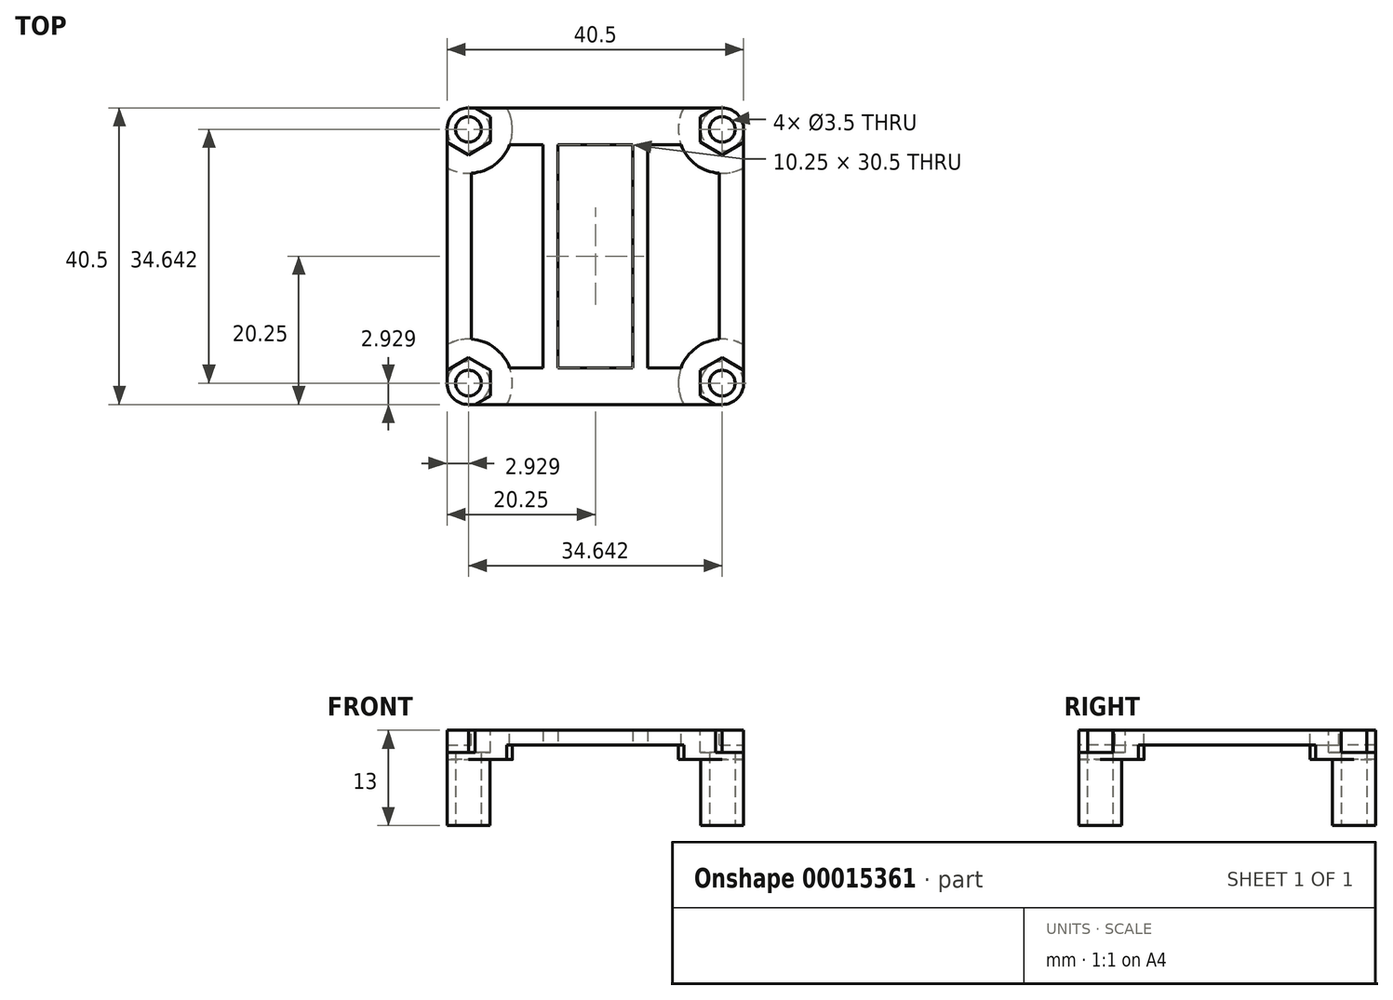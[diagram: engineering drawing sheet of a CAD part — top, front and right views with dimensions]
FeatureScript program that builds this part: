
annotation { "Feature Type Name" : "Feature", "Feature Type Description" : "" }
export const myFeature = defineFeature(function(context is Context, id is Id, definition is map)
    precondition{}
    {
        {
            var Q0;
            Q0=qCreatedBy(makeId("Top.planeOp"),FACE);
            var sketch = newSketch(context, id + "F0", { "sketchPlane" : qUnion([Q0])});
            skLineSegment(sketch, "E0.bottom", {"start": v(2.93, 0) * mm, "end": v(37.57, 0) * mm});
            skLineSegment(sketch, "E0.top", {"start": v(2.93, 40.5) * mm, "end": v(37.57, 40.5) * mm});
            skLineSegment(sketch, "E0.left", {"start": v(0, 2.93) * mm, "end": v(0, 37.57) * mm});
            skLineSegment(sketch, "E0.right", {"start": v(40.5, 2.93) * mm, "end": v(40.5, 37.57) * mm});
            skLineSegment(sketch, "E1", {"start": v(2.93, 0) * mm, "end": v(5, 0) * mm, "construction": true});
            skLineSegment(sketch, "E2", {"start": v(5, 0) * mm, "end": v(5, 5) * mm, "construction": true});
            skLineSegment(sketch, "E3", {"start": v(40.5, 0) * mm, "end": v(0, 40.5) * mm, "construction": true});
            skLineSegment(sketch, "E4.MirrorCS", {"start": v(40.5, 35.5) * mm, "end": v(35.5, 35.5) * mm, "construction": true});
            skLineSegment(sketch, "E5.MirrorCS", {"start": v(40.5, 37.57) * mm, "end": v(40.5, 35.5) * mm, "construction": true});
            skLineSegment(sketch, "E6.bottom", {"start": v(5, 5) * mm, "end": v(35.5, 5) * mm});
            skLineSegment(sketch, "E6.top", {"start": v(5, 35.5) * mm, "end": v(35.5, 35.5) * mm});
            skLineSegment(sketch, "E6.left", {"start": v(5, 5) * mm, "end": v(5, 35.5) * mm, "construction": true});
            skLineSegment(sketch, "E6.right", {"start": v(35.5, 5) * mm, "end": v(35.5, 35.5) * mm, "construction": true});
            skLineSegment(sketch, "E7", {"start": v(5, 35.5) * mm, "end": v(0, 40.5) * mm, "construction": true});
            skCircle(sketch, "E8", {"center": v(2.93, 37.57) * mm, "radius": 2.93 * mm});
            skLineSegment(sketch, "E9", {"start": v(35.5, 35.5) * mm, "end": v(40.5, 40.5) * mm, "construction": true});
            skLineSegment(sketch, "E10", {"start": v(35.5, 5) * mm, "end": v(40.5, 0) * mm, "construction": true});
            skLineSegment(sketch, "E11", {"start": v(5, 5) * mm, "end": v(0, 0) * mm, "construction": true});
            skCircle(sketch, "E12", {"center": v(37.57, 37.57) * mm, "radius": 2.93 * mm});
            skCircle(sketch, "E13", {"center": v(37.57, 2.93) * mm, "radius": 2.93 * mm});
            skCircle(sketch, "E14", {"center": v(2.93, 2.93) * mm, "radius": 2.93 * mm});
            skPoint(sketch, "E15.orphan", {"position": v(40.5, 40.5) * mm});
            skLineSegment(sketch, "E16", {"start": v(3.3, 34.67) * mm, "end": v(3.3, 5.83) * mm});
            skLineSegment(sketch, "E17", {"start": v(3.3, 8.58) * mm, "end": v(0, 8.58) * mm});
            skLineSegment(sketch, "E18", {"start": v(20.25, 40.5) * mm, "end": v(20.25, 0) * mm, "construction": true});
            skLineSegment(sketch, "E19.MirrorCS", {"start": v(37.2, 34.67) * mm, "end": v(37.2, 5.83) * mm});
            skSolve(sketch);
        }
        {
            var Q0;
            Q0=qSketchRegion(id+"F0",true);
            extrude(context, id + "F1", {"entities" : qUnion([Q0]), "depth" : 2 * mm});
        }
        {
            var Q0;
            Q0=makeQuery(id+"F1.opExtrude","CAP_FACE",FACE,{"disambiguationData":[OSD([sQuery(id+"F0.wireOp",EDGE,"E0.bottom"),sQuery(id+"F0.wireOp",EDGE,"E0.top"),sQuery(id+"F0.wireOp",EDGE,"E0.left"),sQuery(id+"F0.wireOp",EDGE,"E0.right"),sQuery(id+"F0.wireOp",EDGE,"E6.bottom"),sQuery(id+"F0.wireOp",EDGE,"E6.top"),sQuery(id+"F0.wireOp",EDGE,"E6.left"),sQuery(id+"F0.wireOp",EDGE,"E6.right"),sQuery(id+"F0.wireOp",EDGE,"E8"),sQuery(id+"F0.wireOp",EDGE,"E12"),sQuery(id+"F0.wireOp",EDGE,"E13"),sQuery(id+"F0.wireOp",EDGE,"E14")])],"isStart":false});
            var sketch = newSketch(context, id + "F2", { "sketchPlane" : qUnion([Q0])});
            skLineSegment(sketch, "E20", {"start": v(35.5, 35.5) * mm, "end": v(40.5, 35.5) * mm, "construction": true});
            skLineSegment(sketch, "E21", {"start": v(25.37, 0) * mm, "end": v(25.37, 17.5) * mm});
            skLineSegment(sketch, "E22", {"start": v(27.37, 0) * mm, "end": v(27.37, 17.5) * mm});
            skLineSegment(sketch, "E23", {"start": v(27.37, 40.5) * mm, "end": v(25.37, 40.5) * mm});
            skLineSegment(sketch, "E24", {"start": v(27.37, 0) * mm, "end": v(25.37, 0) * mm});
            skLineSegment(sketch, "E25", {"start": v(15.12, 0) * mm, "end": v(15.12, 17.5) * mm});
            skLineSegment(sketch, "E26", {"start": v(13.12, 0) * mm, "end": v(13.12, 17.5) * mm});
            skLineSegment(sketch, "E27", {"start": v(15.12, 0) * mm, "end": v(13.12, 0) * mm});
            skLineSegment(sketch, "E28.trimOffspring", {"start": v(25.37, 22.5) * mm, "end": v(25.37, 40.5) * mm});
            skLineSegment(sketch, "E29.trimOffspring", {"start": v(27.37, 22.5) * mm, "end": v(27.37, 40.5) * mm});
            skLineSegment(sketch, "E30", {"start": v(27.37, 5) * mm, "end": v(25.37, 5) * mm, "construction": true});
            skLineSegment(sketch, "E31", {"start": v(13.12, 17.5) * mm, "end": v(13.12, 22.5) * mm});
            skLineSegment(sketch, "E32", {"start": v(15.12, 22.5) * mm, "end": v(15.12, 17.5) * mm});
            skLineSegment(sketch, "E33", {"start": v(25.37, 17.5) * mm, "end": v(25.37, 22.5) * mm});
            skLineSegment(sketch, "E34", {"start": v(27.37, 22.5) * mm, "end": v(27.37, 17.5) * mm});
            skLineSegment(sketch, "E35", {"start": v(25.37, 0) * mm, "end": v(20.25, 0) * mm, "construction": true});
            skLineSegment(sketch, "E36", {"start": v(15.12, 0) * mm, "end": v(20.25, 0) * mm, "construction": true});
            skLineSegment(sketch, "E37", {"start": v(32.5, 0) * mm, "end": v(27.37, 0) * mm, "construction": true});
            skLineSegment(sketch, "E38", {"start": v(25.37, 0) * mm, "end": v(20.25, 0) * mm});
            skLineSegment(sketch, "E39", {"start": v(20.25, 0) * mm, "end": v(15.12, 0) * mm});
            skLineSegment(sketch, "E40", {"start": v(13.12, 0) * mm, "end": v(8, 0) * mm, "construction": true});
            skLineSegment(sketch, "E41", {"start": v(15.12, 22.5) * mm, "end": v(15.12, 40.5) * mm});
            skLineSegment(sketch, "E42", {"start": v(13.12, 22.5) * mm, "end": v(13.12, 40.5) * mm});
            skLineSegment(sketch, "E43", {"start": v(13.12, 40.5) * mm, "end": v(15.12, 40.5) * mm});
            skSolve(sketch);
        }
        {
            var Q0;
            Q0=qSketchRegion(id+"F2",true);
            extrude(context, id + "F3", {"entities" : qUnion([Q0]), "operationType" : NewBodyOperationType.ADD, "oppositeDirection" : true, "depth" : 2 * mm});
        }
        {
            var Q0;
            Q0=makeQuery(id+"F3.boolean.opBoolean","MERGE",FACE,{"derivedFrom":[makeQuery(id+"F1.opExtrude","CAP_FACE",FACE,{"disambiguationData":[OSD([sQuery(id+"F0.wireOp",EDGE,"E0.bottom"),sQuery(id+"F0.wireOp",EDGE,"E0.top"),sQuery(id+"F0.wireOp",EDGE,"E0.left"),sQuery(id+"F0.wireOp",EDGE,"E0.right"),sQuery(id+"F0.wireOp",EDGE,"E6.bottom"),sQuery(id+"F0.wireOp",EDGE,"E6.top"),sQuery(id+"F0.wireOp",EDGE,"E6.left"),sQuery(id+"F0.wireOp",EDGE,"E6.right"),sQuery(id+"F0.wireOp",EDGE,"E8"),sQuery(id+"F0.wireOp",EDGE,"E12"),sQuery(id+"F0.wireOp",EDGE,"E13"),sQuery(id+"F0.wireOp",EDGE,"E14")])],"isStart":true}),makeQuery(id+"F3.opExtrude","CAP_FACE",FACE,{"disambiguationData":[OSD([sQuery(id+"F2.wireOp",EDGE,"c7da8dac-bc2a-4405-bfd0-97204010a069"),sQuery(id+"F2.wireOp",EDGE,"9790cc3b-b639-4113-a787-7c0d9723f163"),sQuery(id+"F2.wireOp",EDGE,"4f99f85e-6439-4b36-988b-b3e9a4bd26c6"),sQuery(id+"F2.wireOp",EDGE,"911e973a-631e-4f16-b688-f4e0a3bfc9f1"),sQuery(id+"F2.wireOp",EDGE,"1fe3dd94-22a9-43b5-bcec-ded061e9c7d3"),sQuery(id+"F2.wireOp",EDGE,"1e1236dd-3a8a-4433-ad9e-4ecfc154d4c1"),sQuery(id+"F2.wireOp",EDGE,"38a01d6c-7896-4c8e-b6a4-e1e4d7deb64a"),sQuery(id+"F2.wireOp",EDGE,"01bc6d42-c53d-48c6-a514-c4a25d82ae2a"),sQuery(id+"F2.wireOp",EDGE,"55cdfa1b-02cf-4525-a6a4-e51ed176019a.trimOffspring"),sQuery(id+"F2.wireOp",EDGE,"bb6cdbd9-6402-45c2-9660-7bda03971079.trimOffspring"),sQuery(id+"F2.wireOp",EDGE,"18632c1b-2427-4a9b-810c-530cddc136f4.trimOffspring"),sQuery(id+"F2.wireOp",EDGE,"b086e4cd-0680-4511-abae-de8535b09383.trimOffspring")])],"isStart":true})]});
            var sketch = newSketch(context, id + "F4", { "sketchPlane" : qUnion([Q0])});
            skCircle(sketch, "E44", {"center": v(37.57, -2.93) * mm, "radius": 2.93 * mm});
            skCircle(sketch, "E45", {"center": v(37.57, -37.57) * mm, "radius": 2.93 * mm});
            skCircle(sketch, "E46", {"center": v(2.93, -37.57) * mm, "radius": 2.93 * mm});
            skCircle(sketch, "E47", {"center": v(2.93, -2.93) * mm, "radius": 2.93 * mm});
            skSolve(sketch);
        }
        {
            var Q0;
            Q0=qSketchRegion(id+"F4",true);
            extrude(context, id + "F5", {"entities" : qUnion([Q0]), "operationType" : NewBodyOperationType.ADD, "depth" : 11 * mm});
        }
        {
            var Q0;
            Q0=makeQuery(id+"F3.boolean.opBoolean","MERGE",FACE,{"derivedFrom":[makeQuery(id+"F1.opExtrude","CAP_FACE",FACE,{"disambiguationData":[OSD([sQuery(id+"F0.wireOp",EDGE,"E0.bottom"),sQuery(id+"F0.wireOp",EDGE,"E0.top"),sQuery(id+"F0.wireOp",EDGE,"E0.left"),sQuery(id+"F0.wireOp",EDGE,"E0.right"),sQuery(id+"F0.wireOp",EDGE,"E6.bottom"),sQuery(id+"F0.wireOp",EDGE,"E6.top"),sQuery(id+"F0.wireOp",EDGE,"E6.left"),sQuery(id+"F0.wireOp",EDGE,"E6.right"),sQuery(id+"F0.wireOp",EDGE,"E8"),sQuery(id+"F0.wireOp",EDGE,"E12"),sQuery(id+"F0.wireOp",EDGE,"E13"),sQuery(id+"F0.wireOp",EDGE,"E14")])],"isStart":true}),makeQuery(id+"F3.opExtrude","CAP_FACE",FACE,{"disambiguationData":[OSD([sQuery(id+"F2.wireOp",EDGE,"c7da8dac-bc2a-4405-bfd0-97204010a069"),sQuery(id+"F2.wireOp",EDGE,"9790cc3b-b639-4113-a787-7c0d9723f163"),sQuery(id+"F2.wireOp",EDGE,"4f99f85e-6439-4b36-988b-b3e9a4bd26c6"),sQuery(id+"F2.wireOp",EDGE,"911e973a-631e-4f16-b688-f4e0a3bfc9f1"),sQuery(id+"F2.wireOp",EDGE,"1fe3dd94-22a9-43b5-bcec-ded061e9c7d3"),sQuery(id+"F2.wireOp",EDGE,"1e1236dd-3a8a-4433-ad9e-4ecfc154d4c1"),sQuery(id+"F2.wireOp",EDGE,"38a01d6c-7896-4c8e-b6a4-e1e4d7deb64a"),sQuery(id+"F2.wireOp",EDGE,"01bc6d42-c53d-48c6-a514-c4a25d82ae2a"),sQuery(id+"F2.wireOp",EDGE,"55cdfa1b-02cf-4525-a6a4-e51ed176019a.trimOffspring"),sQuery(id+"F2.wireOp",EDGE,"bb6cdbd9-6402-45c2-9660-7bda03971079.trimOffspring"),sQuery(id+"F2.wireOp",EDGE,"18632c1b-2427-4a9b-810c-530cddc136f4.trimOffspring"),sQuery(id+"F2.wireOp",EDGE,"b086e4cd-0680-4511-abae-de8535b09383.trimOffspring")])],"isStart":true})]});
            var sketch = newSketch(context, id + "F6", { "sketchPlane" : qUnion([Q0])});
            skCircle(sketch, "E48", {"center": v(37.57, -2.93) * mm, "radius": 1.75 * mm});
            skCircle(sketch, "E49", {"center": v(37.57, -37.57) * mm, "radius": 1.75 * mm});
            skCircle(sketch, "E50", {"center": v(2.93, -37.57) * mm, "radius": 1.75 * mm});
            skCircle(sketch, "E51", {"center": v(2.93, -2.93) * mm, "radius": 1.75 * mm});
            skSolve(sketch);
        }
        {
            var Q0;
            Q0=qSketchRegion(id+"F6",true);
            extrude(context, id + "F7", {"entities" : qUnion([Q0]), "operationType" : NewBodyOperationType.REMOVE, "oppositeDirection" : true, "depth" : 20 * mm, "hasSecondDirection" : true, "secondDirectionOppositeDirection" : false, "secondDirectionDepth" : 20 * mm});
        }
        {
            var Q0;
            Q0=makeQuery(id+"F3.boolean.opBoolean","MERGE",FACE,{"derivedFrom":[makeQuery(id+"F1.opExtrude","CAP_FACE",FACE,{"disambiguationData":[OSD([sQuery(id+"F0.wireOp",EDGE,"E0.bottom"),sQuery(id+"F0.wireOp",EDGE,"E0.top"),sQuery(id+"F0.wireOp",EDGE,"E0.left"),sQuery(id+"F0.wireOp",EDGE,"E0.right"),sQuery(id+"F0.wireOp",EDGE,"E6.bottom"),sQuery(id+"F0.wireOp",EDGE,"E6.top"),sQuery(id+"F0.wireOp",EDGE,"E6.left"),sQuery(id+"F0.wireOp",EDGE,"E6.right"),sQuery(id+"F0.wireOp",EDGE,"E8"),sQuery(id+"F0.wireOp",EDGE,"E12"),sQuery(id+"F0.wireOp",EDGE,"E13"),sQuery(id+"F0.wireOp",EDGE,"E14")])],"isStart":false}),makeQuery(id+"F3.opExtrude","CAP_FACE",FACE,{"disambiguationData":[OSD([sQuery(id+"F2.wireOp",EDGE,"c7da8dac-bc2a-4405-bfd0-97204010a069"),sQuery(id+"F2.wireOp",EDGE,"9790cc3b-b639-4113-a787-7c0d9723f163"),sQuery(id+"F2.wireOp",EDGE,"4f99f85e-6439-4b36-988b-b3e9a4bd26c6"),sQuery(id+"F2.wireOp",EDGE,"911e973a-631e-4f16-b688-f4e0a3bfc9f1"),sQuery(id+"F2.wireOp",EDGE,"1fe3dd94-22a9-43b5-bcec-ded061e9c7d3"),sQuery(id+"F2.wireOp",EDGE,"1e1236dd-3a8a-4433-ad9e-4ecfc154d4c1"),sQuery(id+"F2.wireOp",EDGE,"38a01d6c-7896-4c8e-b6a4-e1e4d7deb64a"),sQuery(id+"F2.wireOp",EDGE,"01bc6d42-c53d-48c6-a514-c4a25d82ae2a"),sQuery(id+"F2.wireOp",EDGE,"55cdfa1b-02cf-4525-a6a4-e51ed176019a.trimOffspring"),sQuery(id+"F2.wireOp",EDGE,"bb6cdbd9-6402-45c2-9660-7bda03971079.trimOffspring"),sQuery(id+"F2.wireOp",EDGE,"18632c1b-2427-4a9b-810c-530cddc136f4.trimOffspring"),sQuery(id+"F2.wireOp",EDGE,"b086e4cd-0680-4511-abae-de8535b09383.trimOffspring")])],"isStart":true})]});
            var sketch = newSketch(context, id + "F8", { "sketchPlane" : qUnion([Q0])});
            skArc(sketch, "E52", {"start": v(2.93, 0) * mm, "mid": v(5, 5) * mm, "end": v(0, 2.93) * mm});
            skArc(sketch, "E53", {"start": v(8.17, 0) * mm, "mid": v(7.17, 7.17) * mm, "end": v(0, 8.17) * mm});
            skLineSegment(sketch, "E54", {"start": v(0, 2.93) * mm, "end": v(0, 8.17) * mm});
            skLineSegment(sketch, "E55", {"start": v(2.93, 0) * mm, "end": v(8.17, 0) * mm});
            skLineSegment(sketch, "E56", {"start": v(0, 20.25) * mm, "end": v(40.5, 20.25) * mm, "construction": true});
            skLineSegment(sketch, "E57", {"start": v(20.25, 0) * mm, "end": v(20.25, 40.5) * mm, "construction": true});
            skArc(sketch, "E58.MirrorCS", {"start": v(32.33, 0) * mm, "mid": v(33.33, 7.17) * mm, "end": v(40.5, 8.17) * mm});
            skArc(sketch, "E59.MirrorCS", {"start": v(37.57, 0) * mm, "mid": v(35.5, 5) * mm, "end": v(40.5, 2.93) * mm});
            skLineSegment(sketch, "E60.MirrorCS", {"start": v(40.5, 2.93) * mm, "end": v(40.5, 8.17) * mm});
            skLineSegment(sketch, "E61.MirrorCS", {"start": v(37.57, 0) * mm, "end": v(32.33, 0) * mm});
            skArc(sketch, "E62.MirrorCS", {"start": v(8.17, 40.5) * mm, "mid": v(7.17, 33.33) * mm, "end": v(0, 32.33) * mm});
            skLineSegment(sketch, "E63.MirrorCS", {"start": v(0, 37.57) * mm, "end": v(0, 32.33) * mm});
            skArc(sketch, "E64.MirrorCS", {"start": v(2.93, 40.5) * mm, "mid": v(5, 35.5) * mm, "end": v(0, 37.57) * mm});
            skLineSegment(sketch, "E65.MirrorCS", {"start": v(2.93, 40.5) * mm, "end": v(8.17, 40.5) * mm});
            skArc(sketch, "E66.MirrorCS", {"start": v(32.33, 40.5) * mm, "mid": v(33.33, 33.33) * mm, "end": v(40.5, 32.33) * mm});
            skLineSegment(sketch, "E67.MirrorCS", {"start": v(40.5, 37.57) * mm, "end": v(40.5, 32.33) * mm});
            skArc(sketch, "E68.MirrorCS", {"start": v(37.57, 40.5) * mm, "mid": v(35.5, 35.5) * mm, "end": v(40.5, 37.57) * mm});
            skLineSegment(sketch, "E69.MirrorCS", {"start": v(37.57, 40.5) * mm, "end": v(32.33, 40.5) * mm});
            skSolve(sketch);
        }
        {
            var Q0;
            Q0=qSketchRegion(id+"F8",true);
            extrude(context, id + "F9", {"entities" : qUnion([Q0]), "operationType" : NewBodyOperationType.ADD, "oppositeDirection" : true, "depth" : 4 * mm});
        }
        {
            var Q0;
            Q0=makeQuery(id+"F9.boolean.opBoolean","MERGE",FACE,{"derivedFrom":[makeQuery(id+"F3.boolean.opBoolean","MERGE",FACE,{"derivedFrom":[makeQuery(id+"F1.opExtrude","CAP_FACE",FACE,{"disambiguationData":[OSD([sQuery(id+"F0.wireOp",EDGE,"E0.bottom"),sQuery(id+"F0.wireOp",EDGE,"E0.top"),sQuery(id+"F0.wireOp",EDGE,"E0.left"),sQuery(id+"F0.wireOp",EDGE,"E0.right"),sQuery(id+"F0.wireOp",EDGE,"E6.bottom"),sQuery(id+"F0.wireOp",EDGE,"E6.top"),sQuery(id+"F0.wireOp",EDGE,"E6.left"),sQuery(id+"F0.wireOp",EDGE,"E6.right"),sQuery(id+"F0.wireOp",EDGE,"E8"),sQuery(id+"F0.wireOp",EDGE,"E12"),sQuery(id+"F0.wireOp",EDGE,"E13"),sQuery(id+"F0.wireOp",EDGE,"E14")])],"isStart":false}),makeQuery(id+"F3.opExtrude","CAP_FACE",FACE,{"disambiguationData":[OSD([sQuery(id+"F2.wireOp",EDGE,"c7da8dac-bc2a-4405-bfd0-97204010a069"),sQuery(id+"F2.wireOp",EDGE,"9790cc3b-b639-4113-a787-7c0d9723f163"),sQuery(id+"F2.wireOp",EDGE,"4f99f85e-6439-4b36-988b-b3e9a4bd26c6"),sQuery(id+"F2.wireOp",EDGE,"911e973a-631e-4f16-b688-f4e0a3bfc9f1"),sQuery(id+"F2.wireOp",EDGE,"1fe3dd94-22a9-43b5-bcec-ded061e9c7d3"),sQuery(id+"F2.wireOp",EDGE,"1e1236dd-3a8a-4433-ad9e-4ecfc154d4c1"),sQuery(id+"F2.wireOp",EDGE,"38a01d6c-7896-4c8e-b6a4-e1e4d7deb64a"),sQuery(id+"F2.wireOp",EDGE,"01bc6d42-c53d-48c6-a514-c4a25d82ae2a"),sQuery(id+"F2.wireOp",EDGE,"55cdfa1b-02cf-4525-a6a4-e51ed176019a.trimOffspring"),sQuery(id+"F2.wireOp",EDGE,"bb6cdbd9-6402-45c2-9660-7bda03971079.trimOffspring"),sQuery(id+"F2.wireOp",EDGE,"18632c1b-2427-4a9b-810c-530cddc136f4.trimOffspring"),sQuery(id+"F2.wireOp",EDGE,"b086e4cd-0680-4511-abae-de8535b09383.trimOffspring")])],"isStart":true})]}),makeQuery(id+"F9.opExtrude","CAP_FACE",FACE,{"disambiguationData":[OSD([sQuery(id+"F8.wireOp",EDGE,"efe3d9ec-0ef8-4ff0-b6d6-6a59cf0e4491"),sQuery(id+"F8.wireOp",EDGE,"64a249c0-91b0-4812-ae5d-63980301e7f1"),sQuery(id+"F8.wireOp",EDGE,"4f005b85-d07d-427a-9fe9-3c07b4558ff1.trimOffspring"),sQuery(id+"F8.wireOp",EDGE,"bc2ab322-11b4-4d09-b126-25cdda3534ac")])],"isStart":true}),makeQuery(id+"F9.opExtrude","CAP_FACE",FACE,{"disambiguationData":[OSD([sQuery(id+"F8.wireOp",EDGE,"4e7f2265-c50e-4890-b22e-6ae81789baec"),sQuery(id+"F8.wireOp",EDGE,"4515257b-2ad8-4fb9-9755-dfa0fcb7d068"),sQuery(id+"F8.wireOp",EDGE,"11088642-985c-47d0-8ebe-78550dc10498.trimOffspring"),sQuery(id+"F8.wireOp",EDGE,"bc85d3af-b0b1-453c-89cb-ee68c843f802")])],"isStart":true}),makeQuery(id+"F9.opExtrude","CAP_FACE",FACE,{"disambiguationData":[OSD([sQuery(id+"F8.wireOp",EDGE,"1842f610-6b7a-4c98-b88b-cc7c31d10b1a"),sQuery(id+"F8.wireOp",EDGE,"f0700d5d-ac5b-4ac4-b89a-0d13518c57df"),sQuery(id+"F8.wireOp",EDGE,"624d2215-cc53-4437-8117-12949c31ea4b.trimOffspring"),sQuery(id+"F8.wireOp",EDGE,"bf0555d9-654c-4ad5-9817-e9fe84b7456e")])],"isStart":true}),makeQuery(id+"F9.opExtrude","CAP_FACE",FACE,{"disambiguationData":[OSD([sQuery(id+"F8.wireOp",EDGE,"5fbfc3d6-65e0-4444-a7b4-bd7d860e697f"),sQuery(id+"F8.wireOp",EDGE,"63d887c8-a1f5-41e6-8b14-20b53bf57f78"),sQuery(id+"F8.wireOp",EDGE,"a6cb9e27-dd16-440d-b453-37740eea144c.trimOffspring"),sQuery(id+"F8.wireOp",EDGE,"ce5d302c-5c8f-45b6-8bb1-96aefa9e179a")])],"isStart":true})]});
            var sketch = newSketch(context, id + "F10", { "sketchPlane" : qUnion([Q0])});
            skCircle(sketch, "E70", {"center": v(2.93, 2.93) * mm, "radius": 3.46 * mm, "construction": true});
            skLineSegment(sketch, "E71", {"start": v(-0.07, 1.2) * mm, "end": v(2.93, -0.54) * mm});
            skLineSegment(sketch, "E72", {"start": v(-0.07, 1.2) * mm, "end": v(-0.07, 4.66) * mm});
            skLineSegment(sketch, "E73", {"start": v(-0.07, 4.66) * mm, "end": v(2.93, -0.54) * mm, "construction": true});
            skLineSegment(sketch, "E74", {"start": v(-0.07, 4.66) * mm, "end": v(2.93, 6.4) * mm});
            skLineSegment(sketch, "E75", {"start": v(2.93, 6.4) * mm, "end": v(5.93, 4.66) * mm});
            skLineSegment(sketch, "E76", {"start": v(5.93, 4.66) * mm, "end": v(-0.07, 4.66) * mm, "construction": true});
            skLineSegment(sketch, "E77", {"start": v(5.93, 4.66) * mm, "end": v(5.93, 1.2) * mm});
            skLineSegment(sketch, "E78", {"start": v(5.93, 1.2) * mm, "end": v(2.93, -0.54) * mm});
            skLineSegment(sketch, "E79", {"start": v(2.93, -0.54) * mm, "end": v(5.93, 4.66) * mm, "construction": true});
            skLineSegment(sketch, "E80", {"start": v(20.25, 0) * mm, "end": v(20.25, 40.5) * mm, "construction": true});
            skLineSegment(sketch, "E81", {"start": v(40.5, 20.25) * mm, "end": v(0, 20.25) * mm, "construction": true});
            skLineSegment(sketch, "E82.MirrorCS", {"start": v(34.57, 1.2) * mm, "end": v(37.57, -0.54) * mm});
            skLineSegment(sketch, "E83.MirrorCS", {"start": v(40.57, 1.2) * mm, "end": v(37.57, -0.54) * mm});
            skLineSegment(sketch, "E84.MirrorCS", {"start": v(40.57, 1.2) * mm, "end": v(40.57, 4.66) * mm});
            skLineSegment(sketch, "E85.MirrorCS", {"start": v(40.57, 4.66) * mm, "end": v(37.57, 6.4) * mm});
            skLineSegment(sketch, "E86.MirrorCS", {"start": v(34.57, 4.66) * mm, "end": v(34.57, 1.2) * mm});
            skLineSegment(sketch, "E87.MirrorCS", {"start": v(37.57, 6.4) * mm, "end": v(34.57, 4.66) * mm});
            skLineSegment(sketch, "E88.MirrorCS", {"start": v(40.57, 35.84) * mm, "end": v(37.57, 34.1) * mm});
            skLineSegment(sketch, "E89.MirrorCS", {"start": v(40.57, 39.3) * mm, "end": v(37.57, 41.04) * mm});
            skLineSegment(sketch, "E90.MirrorCS", {"start": v(40.57, 39.3) * mm, "end": v(40.57, 35.84) * mm});
            skLineSegment(sketch, "E91.MirrorCS", {"start": v(34.57, 35.84) * mm, "end": v(34.57, 39.3) * mm});
            skLineSegment(sketch, "E92.MirrorCS", {"start": v(34.57, 39.3) * mm, "end": v(37.57, 41.04) * mm});
            skLineSegment(sketch, "E93.MirrorCS", {"start": v(37.57, 34.1) * mm, "end": v(34.57, 35.84) * mm});
            skLineSegment(sketch, "E94.MirrorCS", {"start": v(20.25, 40.5) * mm, "end": v(20.25, 0) * mm, "construction": true});
            skLineSegment(sketch, "E95.MirrorCS", {"start": v(-0.07, 39.3) * mm, "end": v(2.93, 41.04) * mm});
            skLineSegment(sketch, "E96.MirrorCS", {"start": v(2.93, 34.1) * mm, "end": v(5.93, 35.84) * mm});
            skLineSegment(sketch, "E97.MirrorCS", {"start": v(-0.07, 39.3) * mm, "end": v(-0.07, 35.84) * mm});
            skLineSegment(sketch, "E98.MirrorCS", {"start": v(-0.07, 35.84) * mm, "end": v(2.93, 34.1) * mm});
            skLineSegment(sketch, "E99.MirrorCS", {"start": v(5.93, 39.3) * mm, "end": v(2.93, 41.04) * mm});
            skLineSegment(sketch, "E100.MirrorCS", {"start": v(5.93, 35.84) * mm, "end": v(5.93, 39.3) * mm});
            skSolve(sketch);
        }
        {
            var Q0;
            Q0=qSketchRegion(id+"F10",true);
            extrude(context, id + "F11", {"entities" : qUnion([Q0]), "operationType" : NewBodyOperationType.REMOVE, "oppositeDirection" : true, "depth" : 3 * mm});
        }
    });
